# Revit family: NLRS_57_AIR_UN_round-jet-diffuser-jtgo-supply LT_sacs
name_source: partatom
category: Air Terminals
units: mm (PartAtom-declared; Revit-internal decimal feet)

## family parameters
Always vertical = Yes
Cut with Voids When Loaded = No
Part Type = Normal
Room Calculation Point = Yes
Round Connector Dimension = Use Diameter
Shared = No
Work Plane-Based = No

## types (4) — shared parameters
Assembly Code = 57.0
Description = Solid Air jet diffuser JTGO (supply)
Manufacturer = Solid Air Climate Systems
Model = Jet diffuser
NLRS_C_content_datum_uitgifte = 26-05-2025
NLRS_C_content_provider = Solid Air Climate Solutions
NLRS_C_content_versie = 4.22.00
NLRS_C_description = Solid Air jet diffuser JTGO (supply)
SACS_Data_Hidden = JTGO_Data
SACS_Data_Hidden2 = JTGO_Factors
URL = https://solid-air.nl

## per-type parameters (varying)
| type | Default Elevation | SACS_Base_Index | SACS_Diameter | SACS_Factor_LpF1 | SACS_Factor_LpF2 | SACS_Factor_PsF1 | SACS_Factor_PsF2 | SACS_Factor_WF1 | SACS_Factor_WF2 |
| JTGOO 160 | 2700 mm  [stored 8.85827 ft] | 1 | 160 mm  [stored 0.524934 ft] | -127.01029 | 26.183073 | 286.689314 | 1.996272 | 0.405084 | 0.55358 |
| JTGOO 200 | 0 mm  [stored 0 ft] | 2 | 200 mm  [stored 0.656168 ft] | -132.764373 | 25.83909 | 139.455855 | 1.997527 | 0.336906 | 0.568318 |
| JTGOO 250 | 0 mm  [stored 0 ft] | 3 | 250 mm  [stored 0.82021 ft] | -146.642993 | 26.17929 | 46.052769 | 1.998901 | 0.320699 | 0.55396 |
| JTGOO 315 | 0 mm  [stored 0 ft] | 4 | 315 mm  [stored 1.03346 ft] | -155.789065 | 25.986197 | 17.342842 | 1.995663 | 0.169358 | 0.621763 |

note: [stored X ft] marks values corroborated as IEEE doubles in the binary element streams (Revit-internal decimal feet)

## geometry (parser evidence)
native form markers: Sweep x12
no freeform markers — native parametric forms only
